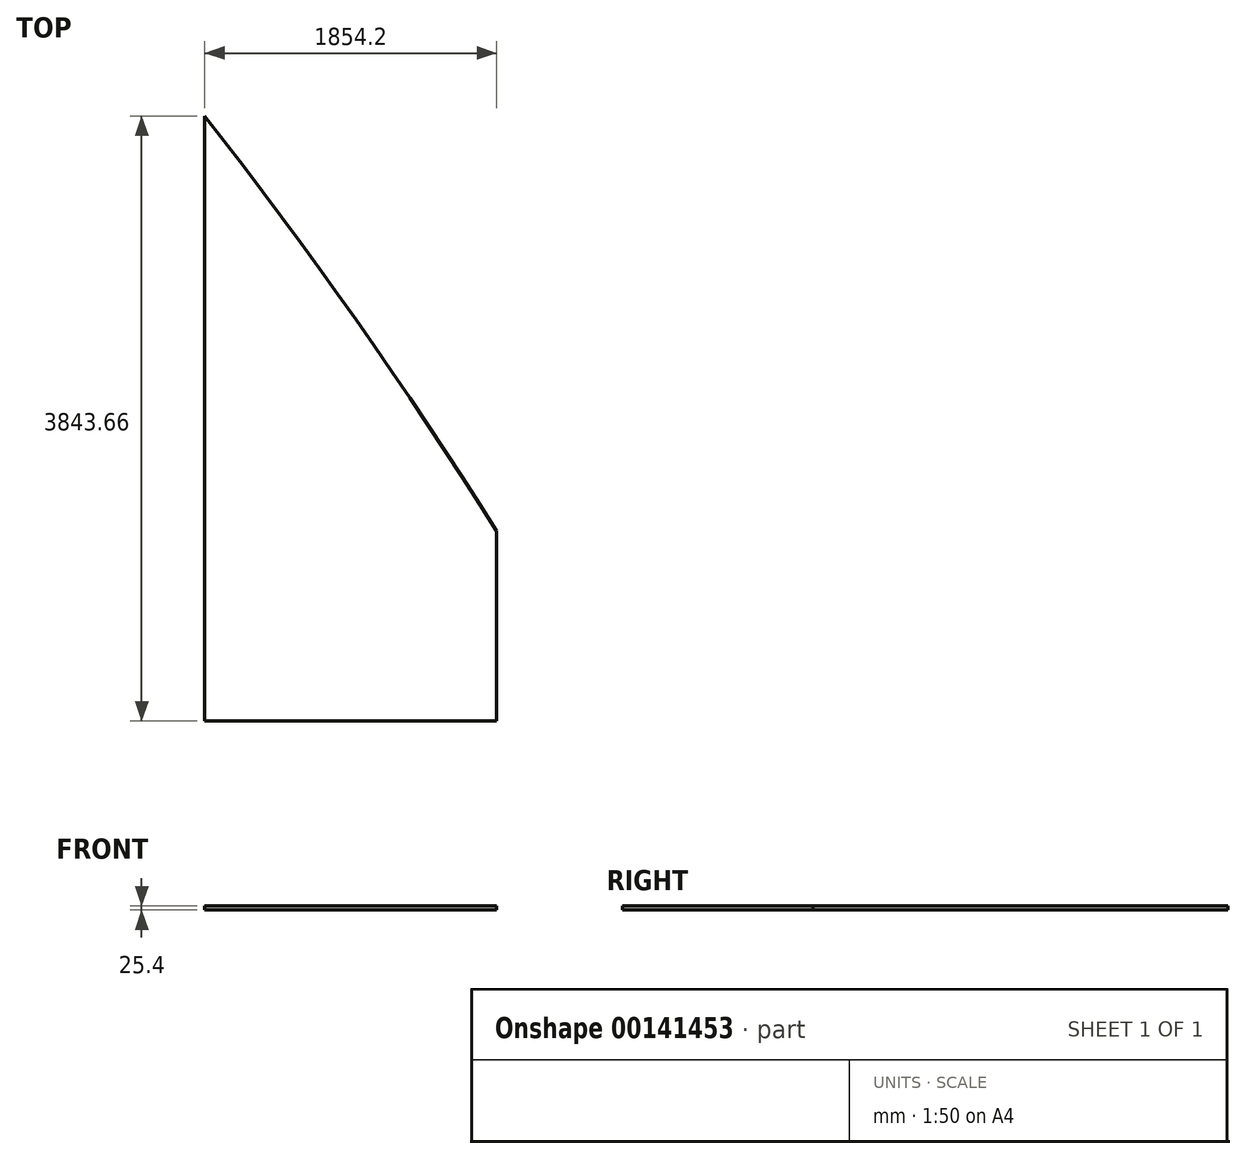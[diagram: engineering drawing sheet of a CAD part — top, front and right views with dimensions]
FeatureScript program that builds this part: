
annotation { "Feature Type Name" : "Feature", "Feature Type Description" : "" }
export const myFeature = defineFeature(function(context is Context, id is Id, definition is map)
    precondition{}
    {
        {
            var Q0;
            Q0=qCreatedBy(makeId("Top.planeOp"),FACE);
            var sketch = newSketch(context, id + "F0", { "sketchPlane" : qUnion([Q0])});
            skLineSegment(sketch, "E0", {"start": v(-817.89, 0) * mm, "end": v(1036.31, 0) * mm});
            skLineSegment(sketch, "E1", {"start": v(-817.89, 0) * mm, "end": v(-817.89, 3843.66) * mm});
            skLineSegment(sketch, "E2", {"start": v(1036.31, 0) * mm, "end": v(1036.31, 1206.88) * mm});
            skArc(sketch, "E3", {"start": v(1036.31, 1206.88) * mm, "mid": v(142.67, 2548.8) * mm, "end": v(-817.89, 3843.65) * mm});
            skSolve(sketch);
        }
        {
            var Q0;
            Q0=makeQuery(id+"F0.imprint","IMPRINT",FACE,{"disambiguationData":[TD([[makeQuery(id+"F0.imprint","IMPRINT",EDGE,{"derivedFrom":sQuery(id+"F0.wireOp",EDGE,"E0")}),1.0]])]});
            extrude(context, id + "F1", {"entities" : qUnion([Q0]), "depth" : 25.4 * mm});
        }
    });
